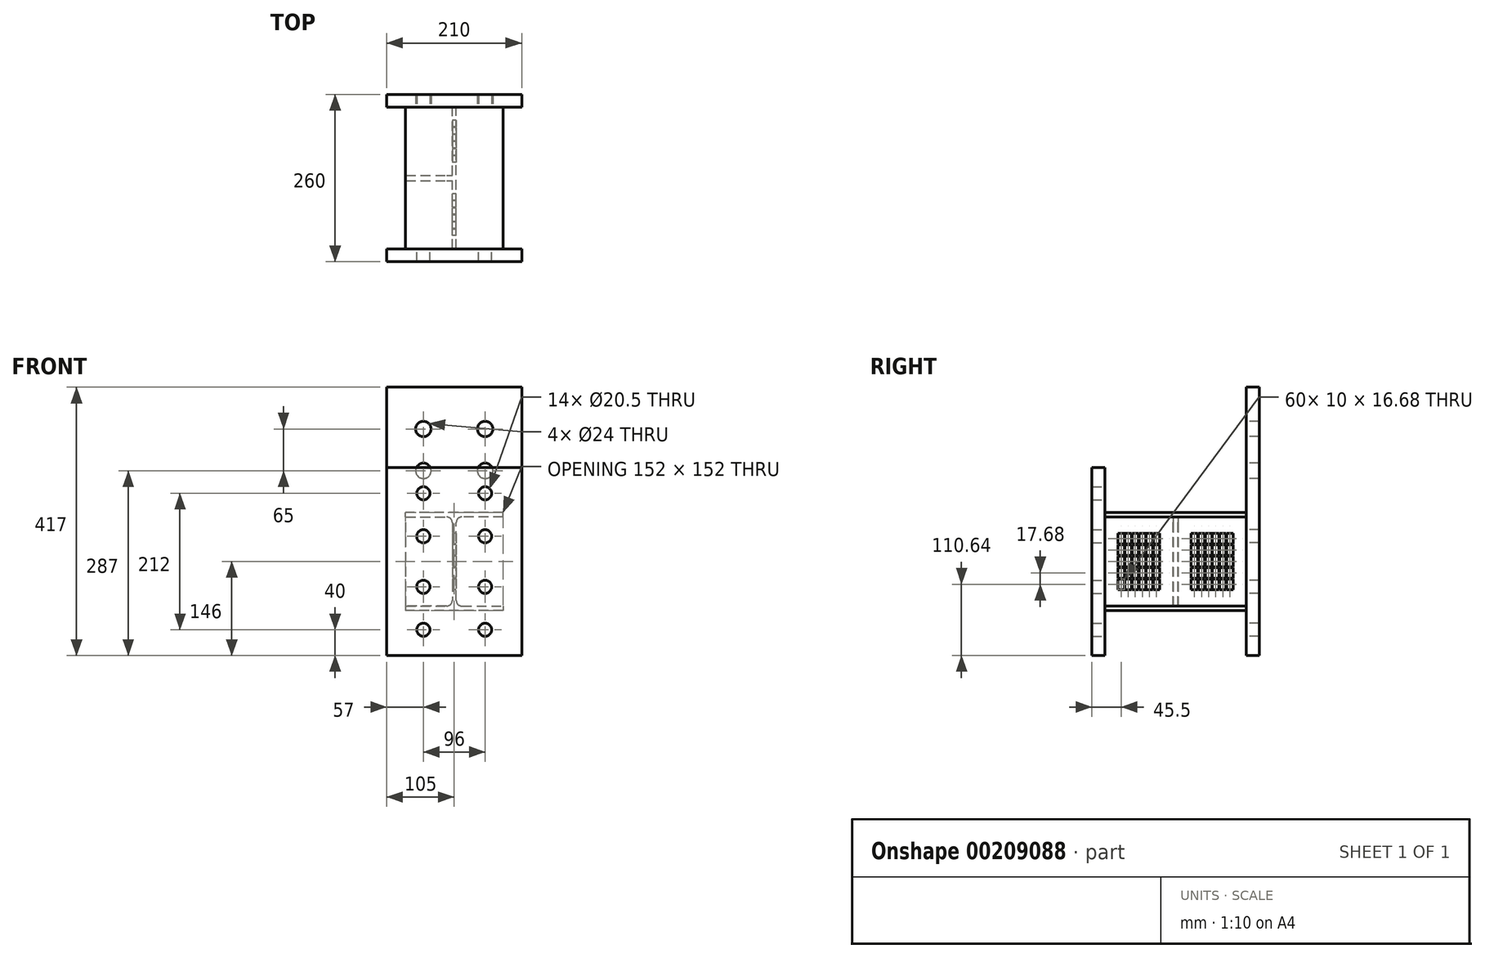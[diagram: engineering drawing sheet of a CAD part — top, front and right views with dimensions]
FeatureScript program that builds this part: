
annotation { "Feature Type Name" : "Feature", "Feature Type Description" : "" }
export const myFeature = defineFeature(function(context is Context, id is Id, definition is map)
    precondition{}
    {
        {
            var Q0;
            Q0=qCreatedBy(makeId("Front.planeOp"),FACE);
            var sketch = newSketch(context, id + "F0", { "sketchPlane" : qUnion([Q0])});
            skLineSegment(sketch, "E0.left", {"start": v(3.05, -60.3) * mm, "end": v(3.05, 60.3) * mm});
            skLineSegment(sketch, "E0.right", {"start": v(-3.05, -60.3) * mm, "end": v(-3.05, 60.3) * mm});
            skPoint(sketch, "E0.middle", {"position": v(0, 0) * mm});
            skLineSegment(sketch, "E1.bottom", {"start": v(76, 69.2) * mm, "end": v(11.95, 69.2) * mm});
            skLineSegment(sketch, "E1.top", {"start": v(76, 76) * mm, "end": v(-76, 76) * mm});
            skLineSegment(sketch, "E1.left", {"start": v(76, 69.2) * mm, "end": v(76, 76) * mm});
            skLineSegment(sketch, "E1.right", {"start": v(-76, 69.2) * mm, "end": v(-76, 76) * mm});
            skLineSegment(sketch, "E2.bottom", {"start": v(-11.95, -69.2) * mm, "end": v(-76, -69.2) * mm});
            skLineSegment(sketch, "E2.top", {"start": v(76, -76) * mm, "end": v(-76, -76) * mm});
            skLineSegment(sketch, "E2.left", {"start": v(76, -69.2) * mm, "end": v(76, -76) * mm});
            skLineSegment(sketch, "E2.right", {"start": v(-76, -69.2) * mm, "end": v(-76, -76) * mm});
            skPoint(sketch, "E3.newPointB", {"position": v(-76, 69.2) * mm});
            skArc(sketch, "E3.filletArc", {"start": v(11.95, 69.2) * mm, "mid": v(5.66, 66.6) * mm, "end": v(3.05, 60.3) * mm});
            skLineSegment(sketch, "E4", {"start": v(-76, 69.2) * mm, "end": v(-11.95, 69.2) * mm});
            skArc(sketch, "E5.filletArc", {"start": v(-3.05, 60.3) * mm, "mid": v(-5.66, 66.6) * mm, "end": v(-11.95, 69.2) * mm});
            skPoint(sketch, "E6.newPointA", {"position": v(76, -69.2) * mm});
            skArc(sketch, "E6.filletArc", {"start": v(-11.95, -69.2) * mm, "mid": v(-5.66, -66.6) * mm, "end": v(-3.05, -60.3) * mm});
            skLineSegment(sketch, "E7", {"start": v(11.95, -69.2) * mm, "end": v(76, -69.2) * mm});
            skArc(sketch, "E8.filletArc", {"start": v(3.05, -60.3) * mm, "mid": v(5.66, -66.6) * mm, "end": v(11.95, -69.2) * mm});
            skSolve(sketch);
        }
        {
            var Q0;
            Q0=qSketchRegion(id+"F0",true);
            extrude(context, id + "F1", {"entities" : qUnion([Q0]), "depth" : 220 * mm, "symmetric" : true});
        }
        {
            var Q0;
            Q0=makeQuery(id+"F1.opExtrude","SWEPT_FACE",FACE,{"disambiguationData":[OSD([sQuery(id+"F0.wireOp",EDGE,"E0.left")])]});
            var sketch = newSketch(context, id + "F2", { "sketchPlane" : qUnion([Q0])});
            skLineSegment(sketch, "E9.bottom", {"start": v(4, -69.2) * mm, "end": v(-4, -69.2) * mm});
            skLineSegment(sketch, "E9.top", {"start": v(4, 69.2) * mm, "end": v(-4, 69.2) * mm});
            skLineSegment(sketch, "E9.left", {"start": v(4, -69.2) * mm, "end": v(4, 69.2) * mm});
            skLineSegment(sketch, "E9.right", {"start": v(-4, -69.2) * mm, "end": v(-4, 69.2) * mm});
            skPoint(sketch, "E9.middle", {"position": v(0, 0) * mm});
            skSolve(sketch);
        }
        {
            var Q0;
            Q0=qSketchRegion(id+"F2",true);
            extrude(context, id + "F3", {"entities" : qUnion([Q0]), "operationType" : NewBodyOperationType.ADD, "oppositeDirection" : true, "depth" : 78.1 * mm});
        }
        {
            var Q0;
            Q0=makeQuery(id+"F1.opExtrude","CAP_FACE",FACE,{"disambiguationData":[OSD([sQuery(id+"F0.wireOp",EDGE,"E0.left"),sQuery(id+"F0.wireOp",EDGE,"E0.right"),sQuery(id+"F0.wireOp",EDGE,"E1.bottom"),sQuery(id+"F0.wireOp",EDGE,"E1.top"),sQuery(id+"F0.wireOp",EDGE,"E1.left"),sQuery(id+"F0.wireOp",EDGE,"E1.right"),sQuery(id+"F0.wireOp",EDGE,"E2.bottom"),sQuery(id+"F0.wireOp",EDGE,"E2.top"),sQuery(id+"F0.wireOp",EDGE,"E2.left"),sQuery(id+"F0.wireOp",EDGE,"E2.right"),sQuery(id+"F0.wireOp",EDGE,"E3.filletArc"),sQuery(id+"F0.wireOp",EDGE,"E4"),sQuery(id+"F0.wireOp",EDGE,"E5.filletArc"),sQuery(id+"F0.wireOp",EDGE,"E6.filletArc"),sQuery(id+"F0.wireOp",EDGE,"E7"),sQuery(id+"F0.wireOp",EDGE,"E8.filletArc")])],"isStart":false});
            var sketch = newSketch(context, id + "F4", { "sketchPlane" : qUnion([Q0])});
            skLineSegment(sketch, "E10.bottom", {"start": v(105, -146) * mm, "end": v(-105, -146) * mm});
            skLineSegment(sketch, "E10.top", {"start": v(105, 146) * mm, "end": v(-105, 146) * mm});
            skLineSegment(sketch, "E10.left", {"start": v(105, -146) * mm, "end": v(105, 146) * mm});
            skLineSegment(sketch, "E10.right", {"start": v(-105, -146) * mm, "end": v(-105, 146) * mm});
            skPoint(sketch, "E10.middle", {"position": v(0, 0) * mm});
            skCircle(sketch, "E11", {"center": v(-48, 106) * mm, "radius": 10.25 * mm});
            skCircle(sketch, "E12", {"center": v(-48, 39.2) * mm, "radius": 10.25 * mm});
            skCircle(sketch, "E13", {"center": v(-48, -39.2) * mm, "radius": 10.25 * mm});
            skCircle(sketch, "E14", {"center": v(-48, -106) * mm, "radius": 10.25 * mm});
            skCircle(sketch, "E15.MirrorC", {"center": v(48, -39.2) * mm, "radius": 10.25 * mm});
            skCircle(sketch, "E16.MirrorC", {"center": v(48, 39.2) * mm, "radius": 10.25 * mm});
            skCircle(sketch, "E17.MirrorC", {"center": v(48, -106) * mm, "radius": 10.25 * mm});
            skCircle(sketch, "E18.MirrorC", {"center": v(48, 106) * mm, "radius": 10.25 * mm});
            skSolve(sketch);
        }
        {
            var Q0;
            Q0=qSketchRegion(id+"F4",true);
            extrude(context, id + "F5", {"entities" : qUnion([Q0]), "operationType" : NewBodyOperationType.ADD, "depth" : 20 * mm});
        }
        {
            var Q0;
            Q0=makeQuery(id+"F1.opExtrude","CAP_FACE",FACE,{"disambiguationData":[OSD([sQuery(id+"F0.wireOp",EDGE,"E0.left"),sQuery(id+"F0.wireOp",EDGE,"E0.right"),sQuery(id+"F0.wireOp",EDGE,"E1.bottom"),sQuery(id+"F0.wireOp",EDGE,"E1.top"),sQuery(id+"F0.wireOp",EDGE,"E1.left"),sQuery(id+"F0.wireOp",EDGE,"E1.right"),sQuery(id+"F0.wireOp",EDGE,"E2.bottom"),sQuery(id+"F0.wireOp",EDGE,"E2.top"),sQuery(id+"F0.wireOp",EDGE,"E2.left"),sQuery(id+"F0.wireOp",EDGE,"E2.right"),sQuery(id+"F0.wireOp",EDGE,"E3.filletArc"),sQuery(id+"F0.wireOp",EDGE,"E4"),sQuery(id+"F0.wireOp",EDGE,"E5.filletArc"),sQuery(id+"F0.wireOp",EDGE,"E6.filletArc"),sQuery(id+"F0.wireOp",EDGE,"E7"),sQuery(id+"F0.wireOp",EDGE,"E8.filletArc")])],"isStart":true});
            var sketch = newSketch(context, id + "F6", { "sketchPlane" : qUnion([Q0])});
            skLineSegment(sketch, "E19.bottom", {"start": v(-105, -146) * mm, "end": v(105, -146) * mm});
            skLineSegment(sketch, "E19.top", {"start": v(-105, 271) * mm, "end": v(105, 271) * mm});
            skLineSegment(sketch, "E19.left", {"start": v(-105, -146) * mm, "end": v(-105, 271) * mm});
            skLineSegment(sketch, "E19.right", {"start": v(105, 271) * mm, "end": v(105, -146) * mm});
            skCircle(sketch, "E20", {"center": v(-48, 39.2) * mm, "radius": 10.25 * mm});
            skCircle(sketch, "E21.MirrorC", {"center": v(-48, -106) * mm, "radius": 10.25 * mm});
            skCircle(sketch, "E22.MirrorC", {"center": v(-48, -39.2) * mm, "radius": 10.25 * mm});
            skLineSegment(sketch, "E23", {"start": v(0, 0) * mm, "end": v(0, 68.37) * mm});
            skPoint(sketch, "E23.endSnap0", {"position": v(0, 76) * mm});
            skCircle(sketch, "E24.MirrorC", {"center": v(48, -106) * mm, "radius": 10.25 * mm});
            skCircle(sketch, "E25.MirrorC", {"center": v(48, -39.2) * mm, "radius": 10.25 * mm});
            skCircle(sketch, "E26.MirrorC", {"center": v(48, 39.2) * mm, "radius": 10.25 * mm});
            skCircle(sketch, "E27", {"center": v(-48, 141) * mm, "radius": 12 * mm});
            skCircle(sketch, "E28", {"center": v(-48, 206) * mm, "radius": 12 * mm});
            skCircle(sketch, "E29.MirrorC", {"center": v(48, 141) * mm, "radius": 12 * mm});
            skCircle(sketch, "E30.MirrorC", {"center": v(48, 206) * mm, "radius": 12 * mm});
            skSolve(sketch);
        }
        {
            var Q0;
            Q0=qSketchRegion(id+"F6",true);
            extrude(context, id + "F7", {"entities" : qUnion([Q0]), "operationType" : NewBodyOperationType.ADD, "depth" : 20 * mm});
        }
        {
            var Q0;
            {var subQ2=sQuery(id+"F0.wireOp",EDGE,"E0.right");Q0=makeQuery(id+"F3.boolean.opBoolean","SPLIT",FACE,{"disambiguationData":[TD([makeQuery(id+"F3.opExtrude","SWEPT_FACE",FACE,{"disambiguationData":[OSD([sQuery(id+"F2.wireOp",EDGE,"E9.left")])]})])],"derivedFrom":makeQuery(id+"F1.opExtrude","SWEPT_FACE",FACE,{"disambiguationData":[OSD([subQ2])]})});}
            var sketch = newSketch(context, id + "F8", { "sketchPlane" : qUnion([Q0])});
            skPoint(sketch, "E31.middle", {"position": v(-57, 0) * mm});
            skPoint(sketch, "E31.middle.positionSnap0", {"position": v(-4, 0) * mm});
            skPoint(sketch, "E31.middle.positionSnap1", {"position": v(-57, 60.3) * mm});
            skPoint(sketch, "E31.centerSnap0", {"position": v(-4, 0) * mm});
            skPoint(sketch, "E31.centerSnap1", {"position": v(-57, 60.3) * mm});
            skPoint(sketch, "E32.MirrorP", {"position": v(-35, 0) * mm});
            skPoint(sketch, "E33.middle", {"position": v(-57, 26.52) * mm});
            skPoint(sketch, "E34.middle", {"position": v(-57, 8.84) * mm});
            skPoint(sketch, "E35.middle", {"position": v(-57, -8.84) * mm});
            skPoint(sketch, "E36.middle", {"position": v(-57, -26.52) * mm});
            skPoint(sketch, "E37.middle", {"position": v(-57, -44.2) * mm});
            skPoint(sketch, "E38.middle", {"position": v(-57, 44.2) * mm});
            skPoint(sketch, "E39.middle", {"position": v(-90, 0) * mm});
            skPoint(sketch, "E40.middle", {"position": v(-79, 0) * mm});
            skPoint(sketch, "E41.middle", {"position": v(-68, 0) * mm});
            skPoint(sketch, "E42.middle", {"position": v(-46, 0) * mm});
            skPoint(sketch, "E43.middle", {"position": v(-24, 0) * mm});
            skLineSegment(sketch, "E44.bottom", {"start": v(-89.5, 43.7) * mm, "end": v(-79.5, 43.7) * mm});
            skLineSegment(sketch, "E44.top", {"start": v(-89.5, 27.02) * mm, "end": v(-79.5, 27.02) * mm});
            skLineSegment(sketch, "E44.left", {"start": v(-89.5, 43.7) * mm, "end": v(-89.5, 27.02) * mm});
            skLineSegment(sketch, "E44.right", {"start": v(-79.5, 43.7) * mm, "end": v(-79.5, 27.02) * mm});
            skLineSegment(sketch, "E45.bottom", {"start": v(-78.5, 43.7) * mm, "end": v(-68.5, 43.7) * mm});
            skLineSegment(sketch, "E45.top", {"start": v(-78.5, 27.02) * mm, "end": v(-68.5, 27.02) * mm});
            skLineSegment(sketch, "E45.left", {"start": v(-78.5, 43.7) * mm, "end": v(-78.5, 27.02) * mm});
            skLineSegment(sketch, "E45.right", {"start": v(-68.5, 43.7) * mm, "end": v(-68.5, 27.02) * mm});
            skLineSegment(sketch, "E46.bottom", {"start": v(-67.5, 43.7) * mm, "end": v(-57.5, 43.7) * mm});
            skLineSegment(sketch, "E46.top", {"start": v(-67.5, 27.02) * mm, "end": v(-57.5, 27.02) * mm});
            skLineSegment(sketch, "E46.left", {"start": v(-67.5, 43.7) * mm, "end": v(-67.5, 27.02) * mm});
            skLineSegment(sketch, "E46.right", {"start": v(-57.5, 43.7) * mm, "end": v(-57.5, 27.02) * mm});
            skLineSegment(sketch, "E47.bottom", {"start": v(-56.5, 43.7) * mm, "end": v(-46.5, 43.7) * mm});
            skLineSegment(sketch, "E47.top", {"start": v(-56.5, 27.02) * mm, "end": v(-46.5, 27.02) * mm});
            skLineSegment(sketch, "E47.left", {"start": v(-56.5, 43.7) * mm, "end": v(-56.5, 27.02) * mm});
            skLineSegment(sketch, "E47.right", {"start": v(-46.5, 43.7) * mm, "end": v(-46.5, 27.02) * mm});
            skLineSegment(sketch, "E48.bottom", {"start": v(-45.5, 43.7) * mm, "end": v(-35.5, 43.7) * mm});
            skLineSegment(sketch, "E48.top", {"start": v(-45.5, 27.02) * mm, "end": v(-35.5, 27.02) * mm});
            skLineSegment(sketch, "E48.left", {"start": v(-45.5, 43.7) * mm, "end": v(-45.5, 27.02) * mm});
            skLineSegment(sketch, "E48.right", {"start": v(-35.5, 43.7) * mm, "end": v(-35.5, 27.02) * mm});
            skLineSegment(sketch, "E49.bottom", {"start": v(-34.5, 43.7) * mm, "end": v(-24.5, 43.7) * mm});
            skLineSegment(sketch, "E49.top", {"start": v(-34.5, 27.02) * mm, "end": v(-24.5, 27.02) * mm});
            skLineSegment(sketch, "E49.left", {"start": v(-34.5, 43.7) * mm, "end": v(-34.5, 27.02) * mm});
            skLineSegment(sketch, "E49.right", {"start": v(-24.5, 43.7) * mm, "end": v(-24.5, 27.02) * mm});
            skLineSegment(sketch, "E50.bottom", {"start": v(-89.5, 26.02) * mm, "end": v(-79.5, 26.02) * mm});
            skLineSegment(sketch, "E50.top", {"start": v(-89.5, 9.34) * mm, "end": v(-79.5, 9.34) * mm});
            skLineSegment(sketch, "E50.left", {"start": v(-89.5, 26.02) * mm, "end": v(-89.5, 9.34) * mm});
            skLineSegment(sketch, "E50.right", {"start": v(-79.5, 26.02) * mm, "end": v(-79.5, 9.34) * mm});
            skLineSegment(sketch, "E51.bottom", {"start": v(-78.5, 26.02) * mm, "end": v(-68.5, 26.02) * mm});
            skLineSegment(sketch, "E51.top", {"start": v(-78.5, 9.34) * mm, "end": v(-68.5, 9.34) * mm});
            skLineSegment(sketch, "E51.left", {"start": v(-78.5, 26.02) * mm, "end": v(-78.5, 9.34) * mm});
            skLineSegment(sketch, "E51.right", {"start": v(-68.5, 26.02) * mm, "end": v(-68.5, 9.34) * mm});
            skLineSegment(sketch, "E52.bottom", {"start": v(-67.5, 26.02) * mm, "end": v(-57.5, 26.02) * mm});
            skLineSegment(sketch, "E52.top", {"start": v(-67.5, 9.34) * mm, "end": v(-57.5, 9.34) * mm});
            skLineSegment(sketch, "E52.left", {"start": v(-67.5, 26.02) * mm, "end": v(-67.5, 9.34) * mm});
            skLineSegment(sketch, "E52.right", {"start": v(-57.5, 26.02) * mm, "end": v(-57.5, 9.34) * mm});
            skLineSegment(sketch, "E53.bottom", {"start": v(-56.5, 26.02) * mm, "end": v(-46.5, 26.02) * mm});
            skLineSegment(sketch, "E53.top", {"start": v(-56.5, 9.34) * mm, "end": v(-46.5, 9.34) * mm});
            skLineSegment(sketch, "E53.left", {"start": v(-56.5, 26.02) * mm, "end": v(-56.5, 9.34) * mm});
            skLineSegment(sketch, "E53.right", {"start": v(-46.5, 26.02) * mm, "end": v(-46.5, 9.34) * mm});
            skLineSegment(sketch, "E54.bottom", {"start": v(-45.5, 26.02) * mm, "end": v(-35.5, 26.02) * mm});
            skLineSegment(sketch, "E54.top", {"start": v(-45.5, 9.34) * mm, "end": v(-35.5, 9.34) * mm});
            skLineSegment(sketch, "E54.left", {"start": v(-45.5, 26.02) * mm, "end": v(-45.5, 9.34) * mm});
            skLineSegment(sketch, "E54.right", {"start": v(-35.5, 26.02) * mm, "end": v(-35.5, 9.34) * mm});
            skLineSegment(sketch, "E55.bottom", {"start": v(-34.5, 26.02) * mm, "end": v(-24.5, 26.02) * mm});
            skLineSegment(sketch, "E55.top", {"start": v(-34.5, 9.34) * mm, "end": v(-24.5, 9.34) * mm});
            skLineSegment(sketch, "E55.left", {"start": v(-34.5, 26.02) * mm, "end": v(-34.5, 9.34) * mm});
            skLineSegment(sketch, "E55.right", {"start": v(-24.5, 26.02) * mm, "end": v(-24.5, 9.34) * mm});
            skLineSegment(sketch, "E56.bottom", {"start": v(-89.5, 8.34) * mm, "end": v(-79.5, 8.34) * mm});
            skLineSegment(sketch, "E56.top", {"start": v(-89.5, -8.34) * mm, "end": v(-79.5, -8.34) * mm});
            skLineSegment(sketch, "E56.left", {"start": v(-89.5, 8.34) * mm, "end": v(-89.5, -8.34) * mm});
            skLineSegment(sketch, "E56.right", {"start": v(-79.5, 8.34) * mm, "end": v(-79.5, -8.34) * mm});
            skLineSegment(sketch, "E57.bottom", {"start": v(-78.5, 8.34) * mm, "end": v(-68.5, 8.34) * mm});
            skLineSegment(sketch, "E57.top", {"start": v(-78.5, -8.34) * mm, "end": v(-68.5, -8.34) * mm});
            skLineSegment(sketch, "E57.left", {"start": v(-78.5, 8.34) * mm, "end": v(-78.5, -8.34) * mm});
            skLineSegment(sketch, "E57.right", {"start": v(-68.5, 8.34) * mm, "end": v(-68.5, -8.34) * mm});
            skLineSegment(sketch, "E58.bottom", {"start": v(-67.5, 8.34) * mm, "end": v(-57.5, 8.34) * mm});
            skLineSegment(sketch, "E58.top", {"start": v(-67.5, -8.34) * mm, "end": v(-57.5, -8.34) * mm});
            skLineSegment(sketch, "E58.left", {"start": v(-67.5, 8.34) * mm, "end": v(-67.5, -8.34) * mm});
            skLineSegment(sketch, "E58.right", {"start": v(-57.5, 8.34) * mm, "end": v(-57.5, -8.34) * mm});
            skLineSegment(sketch, "E59.bottom", {"start": v(-56.5, 8.34) * mm, "end": v(-46.5, 8.34) * mm});
            skLineSegment(sketch, "E59.top", {"start": v(-56.5, -8.34) * mm, "end": v(-46.5, -8.34) * mm});
            skLineSegment(sketch, "E59.left", {"start": v(-56.5, 8.34) * mm, "end": v(-56.5, -8.34) * mm});
            skLineSegment(sketch, "E59.right", {"start": v(-46.5, 8.34) * mm, "end": v(-46.5, -8.34) * mm});
            skLineSegment(sketch, "E60.bottom", {"start": v(-45.5, 8.34) * mm, "end": v(-35.5, 8.34) * mm});
            skLineSegment(sketch, "E60.top", {"start": v(-45.5, -8.34) * mm, "end": v(-35.5, -8.34) * mm});
            skLineSegment(sketch, "E60.left", {"start": v(-45.5, 8.34) * mm, "end": v(-45.5, -8.34) * mm});
            skLineSegment(sketch, "E60.right", {"start": v(-35.5, 8.34) * mm, "end": v(-35.5, -8.34) * mm});
            skLineSegment(sketch, "E61.bottom", {"start": v(-34.5, 8.34) * mm, "end": v(-24.5, 8.34) * mm});
            skLineSegment(sketch, "E61.top", {"start": v(-34.5, -8.34) * mm, "end": v(-24.5, -8.34) * mm});
            skLineSegment(sketch, "E61.left", {"start": v(-34.5, 8.34) * mm, "end": v(-34.5, -8.34) * mm});
            skLineSegment(sketch, "E61.right", {"start": v(-24.5, 8.34) * mm, "end": v(-24.5, -8.34) * mm});
            skLineSegment(sketch, "E62.bottom", {"start": v(-89.5, -9.34) * mm, "end": v(-79.5, -9.34) * mm});
            skLineSegment(sketch, "E62.top", {"start": v(-89.5, -26.02) * mm, "end": v(-79.5, -26.02) * mm});
            skLineSegment(sketch, "E62.left", {"start": v(-89.5, -9.34) * mm, "end": v(-89.5, -26.02) * mm});
            skLineSegment(sketch, "E62.right", {"start": v(-79.5, -9.34) * mm, "end": v(-79.5, -26.02) * mm});
            skLineSegment(sketch, "E63.bottom", {"start": v(-78.5, -9.34) * mm, "end": v(-68.5, -9.34) * mm});
            skLineSegment(sketch, "E63.top", {"start": v(-78.5, -26.02) * mm, "end": v(-68.5, -26.02) * mm});
            skLineSegment(sketch, "E63.left", {"start": v(-78.5, -9.34) * mm, "end": v(-78.5, -26.02) * mm});
            skLineSegment(sketch, "E63.right", {"start": v(-68.5, -9.34) * mm, "end": v(-68.5, -26.02) * mm});
            skLineSegment(sketch, "E64.bottom", {"start": v(-67.5, -9.34) * mm, "end": v(-57.5, -9.34) * mm});
            skLineSegment(sketch, "E64.top", {"start": v(-67.5, -26.02) * mm, "end": v(-57.5, -26.02) * mm});
            skLineSegment(sketch, "E64.left", {"start": v(-67.5, -9.34) * mm, "end": v(-67.5, -26.02) * mm});
            skLineSegment(sketch, "E64.right", {"start": v(-57.5, -9.34) * mm, "end": v(-57.5, -26.02) * mm});
            skLineSegment(sketch, "E65.bottom", {"start": v(-56.5, -9.34) * mm, "end": v(-46.5, -9.34) * mm});
            skLineSegment(sketch, "E65.top", {"start": v(-56.5, -26.02) * mm, "end": v(-46.5, -26.02) * mm});
            skLineSegment(sketch, "E65.left", {"start": v(-56.5, -9.34) * mm, "end": v(-56.5, -26.02) * mm});
            skLineSegment(sketch, "E65.right", {"start": v(-46.5, -9.34) * mm, "end": v(-46.5, -26.02) * mm});
            skLineSegment(sketch, "E66.bottom", {"start": v(-45.5, -9.34) * mm, "end": v(-35.5, -9.34) * mm});
            skLineSegment(sketch, "E66.top", {"start": v(-45.5, -26.02) * mm, "end": v(-35.5, -26.02) * mm});
            skLineSegment(sketch, "E66.left", {"start": v(-45.5, -9.34) * mm, "end": v(-45.5, -26.02) * mm});
            skLineSegment(sketch, "E66.right", {"start": v(-35.5, -9.34) * mm, "end": v(-35.5, -26.02) * mm});
            skLineSegment(sketch, "E67.bottom", {"start": v(-34.5, -9.34) * mm, "end": v(-24.5, -9.34) * mm});
            skLineSegment(sketch, "E67.top", {"start": v(-34.5, -26.02) * mm, "end": v(-24.5, -26.02) * mm});
            skLineSegment(sketch, "E67.left", {"start": v(-34.5, -9.34) * mm, "end": v(-34.5, -26.02) * mm});
            skLineSegment(sketch, "E67.right", {"start": v(-24.5, -9.34) * mm, "end": v(-24.5, -26.02) * mm});
            skLineSegment(sketch, "E68.bottom", {"start": v(-89.5, -27.02) * mm, "end": v(-79.5, -27.02) * mm});
            skLineSegment(sketch, "E68.top", {"start": v(-89.5, -43.7) * mm, "end": v(-79.5, -43.7) * mm});
            skLineSegment(sketch, "E68.left", {"start": v(-89.5, -27.02) * mm, "end": v(-89.5, -43.7) * mm});
            skLineSegment(sketch, "E68.right", {"start": v(-79.5, -27.02) * mm, "end": v(-79.5, -43.7) * mm});
            skLineSegment(sketch, "E69.bottom", {"start": v(-78.5, -27.02) * mm, "end": v(-68.5, -27.02) * mm});
            skLineSegment(sketch, "E69.top", {"start": v(-78.5, -43.7) * mm, "end": v(-68.5, -43.7) * mm});
            skLineSegment(sketch, "E69.left", {"start": v(-78.5, -27.02) * mm, "end": v(-78.5, -43.7) * mm});
            skLineSegment(sketch, "E69.right", {"start": v(-68.5, -27.02) * mm, "end": v(-68.5, -43.7) * mm});
            skLineSegment(sketch, "E70.bottom", {"start": v(-67.5, -27.02) * mm, "end": v(-57.5, -27.02) * mm});
            skLineSegment(sketch, "E70.top", {"start": v(-67.5, -43.7) * mm, "end": v(-57.5, -43.7) * mm});
            skLineSegment(sketch, "E70.left", {"start": v(-67.5, -27.02) * mm, "end": v(-67.5, -43.7) * mm});
            skLineSegment(sketch, "E70.right", {"start": v(-57.5, -27.02) * mm, "end": v(-57.5, -43.7) * mm});
            skLineSegment(sketch, "E71.bottom", {"start": v(-56.5, -27.02) * mm, "end": v(-46.5, -27.02) * mm});
            skLineSegment(sketch, "E71.top", {"start": v(-56.5, -43.7) * mm, "end": v(-46.5, -43.7) * mm});
            skLineSegment(sketch, "E71.left", {"start": v(-56.5, -27.02) * mm, "end": v(-56.5, -43.7) * mm});
            skLineSegment(sketch, "E71.right", {"start": v(-46.5, -27.02) * mm, "end": v(-46.5, -43.7) * mm});
            skLineSegment(sketch, "E72.bottom", {"start": v(-45.5, -27.02) * mm, "end": v(-35.5, -27.02) * mm});
            skLineSegment(sketch, "E72.top", {"start": v(-45.5, -43.7) * mm, "end": v(-35.5, -43.7) * mm});
            skLineSegment(sketch, "E72.left", {"start": v(-45.5, -27.02) * mm, "end": v(-45.5, -43.7) * mm});
            skLineSegment(sketch, "E72.right", {"start": v(-35.5, -27.02) * mm, "end": v(-35.5, -43.7) * mm});
            skLineSegment(sketch, "E73.bottom", {"start": v(-34.5, -27.02) * mm, "end": v(-24.5, -27.02) * mm});
            skLineSegment(sketch, "E73.top", {"start": v(-34.5, -43.7) * mm, "end": v(-24.5, -43.7) * mm});
            skLineSegment(sketch, "E73.left", {"start": v(-34.5, -27.02) * mm, "end": v(-34.5, -43.7) * mm});
            skLineSegment(sketch, "E73.right", {"start": v(-24.5, -27.02) * mm, "end": v(-24.5, -43.7) * mm});
            skLineSegment(sketch, "E74", {"start": v(0, 60.3) * mm, "end": v(0, -69) * mm});
            skLineSegment(sketch, "E75.MirrorCS", {"start": v(35.5, 8.34) * mm, "end": v(35.5, -8.34) * mm});
            skLineSegment(sketch, "E76.MirrorCS", {"start": v(79.5, 8.34) * mm, "end": v(79.5, -8.34) * mm});
            skLineSegment(sketch, "E77.MirrorCS", {"start": v(57.5, 8.34) * mm, "end": v(57.5, -8.34) * mm});
            skLineSegment(sketch, "E78.MirrorCS", {"start": v(34.5, 8.34) * mm, "end": v(34.5, -8.34) * mm});
            skLineSegment(sketch, "E79.MirrorCS", {"start": v(67.5, -27.02) * mm, "end": v(57.5, -27.02) * mm});
            skLineSegment(sketch, "E80.MirrorCS", {"start": v(56.5, 8.34) * mm, "end": v(56.5, -8.34) * mm});
            skLineSegment(sketch, "E81.MirrorCS", {"start": v(45.5, 8.34) * mm, "end": v(45.5, -8.34) * mm});
            skLineSegment(sketch, "E82.MirrorCS", {"start": v(89.5, 8.34) * mm, "end": v(89.5, -8.34) * mm});
            skPoint(sketch, "E83.MirrorP", {"position": v(57, 0) * mm});
            skLineSegment(sketch, "E84.MirrorCS", {"start": v(79.5, 43.7) * mm, "end": v(79.5, 27.02) * mm});
            skLineSegment(sketch, "E85.MirrorCS", {"start": v(67.5, 43.7) * mm, "end": v(57.5, 43.7) * mm});
            skLineSegment(sketch, "E86.MirrorCS", {"start": v(67.5, 27.02) * mm, "end": v(57.5, 27.02) * mm});
            skLineSegment(sketch, "E87.MirrorCS", {"start": v(79.5, -27.02) * mm, "end": v(79.5, -43.7) * mm});
            skPoint(sketch, "E88.MirrorP", {"position": v(35, 0) * mm});
            skLineSegment(sketch, "E89.MirrorCS", {"start": v(34.5, -27.02) * mm, "end": v(24.5, -27.02) * mm});
            skLineSegment(sketch, "E90.MirrorCS", {"start": v(78.5, -27.02) * mm, "end": v(68.5, -27.02) * mm});
            skLineSegment(sketch, "E91.MirrorCS", {"start": v(56.5, -26.02) * mm, "end": v(46.5, -26.02) * mm});
            skLineSegment(sketch, "E92.MirrorCS", {"start": v(78.5, 8.34) * mm, "end": v(78.5, -8.34) * mm});
            skLineSegment(sketch, "E93.MirrorCS", {"start": v(24.5, 8.34) * mm, "end": v(24.5, -8.34) * mm});
            skLineSegment(sketch, "E94.MirrorCS", {"start": v(68.5, 8.34) * mm, "end": v(68.5, -8.34) * mm});
            skLineSegment(sketch, "E95.MirrorCS", {"start": v(67.5, 8.34) * mm, "end": v(57.5, 8.34) * mm});
            skLineSegment(sketch, "E96.MirrorCS", {"start": v(89.5, -26.02) * mm, "end": v(79.5, -26.02) * mm});
            skLineSegment(sketch, "E97.MirrorCS", {"start": v(67.5, -8.34) * mm, "end": v(57.5, -8.34) * mm});
            skLineSegment(sketch, "E98.MirrorCS", {"start": v(67.5, -43.7) * mm, "end": v(57.5, -43.7) * mm});
            skLineSegment(sketch, "E99.MirrorCS", {"start": v(45.5, -26.02) * mm, "end": v(35.5, -26.02) * mm});
            skLineSegment(sketch, "E100.MirrorCS", {"start": v(67.5, 8.34) * mm, "end": v(67.5, -8.34) * mm});
            skLineSegment(sketch, "E101.MirrorCS", {"start": v(79.5, -9.34) * mm, "end": v(79.5, -26.02) * mm});
            skLineSegment(sketch, "E102.MirrorCS", {"start": v(79.5, 26.02) * mm, "end": v(79.5, 9.34) * mm});
            skLineSegment(sketch, "E103.MirrorCS", {"start": v(46.5, 8.34) * mm, "end": v(46.5, -8.34) * mm});
            skLineSegment(sketch, "E104.MirrorCS", {"start": v(67.5, 26.02) * mm, "end": v(57.5, 26.02) * mm});
            skLineSegment(sketch, "E105.MirrorCS", {"start": v(67.5, -9.34) * mm, "end": v(57.5, -9.34) * mm});
            skLineSegment(sketch, "E106.MirrorCS", {"start": v(67.5, 9.34) * mm, "end": v(57.5, 9.34) * mm});
            skLineSegment(sketch, "E107.MirrorCS", {"start": v(67.5, -26.02) * mm, "end": v(57.5, -26.02) * mm});
            skLineSegment(sketch, "E108.MirrorCS", {"start": v(67.5, 26.02) * mm, "end": v(67.5, 9.34) * mm});
            skLineSegment(sketch, "E109.MirrorCS", {"start": v(45.5, 43.7) * mm, "end": v(45.5, 27.02) * mm});
            skLineSegment(sketch, "E110.MirrorCS", {"start": v(89.5, -27.02) * mm, "end": v(89.5, -43.7) * mm});
            skLineSegment(sketch, "E111.MirrorCS", {"start": v(67.5, -9.34) * mm, "end": v(67.5, -26.02) * mm});
            skLineSegment(sketch, "E112.MirrorCS", {"start": v(45.5, -27.02) * mm, "end": v(45.5, -43.7) * mm});
            skLineSegment(sketch, "E113.MirrorCS", {"start": v(56.5, 27.02) * mm, "end": v(46.5, 27.02) * mm});
            skLineSegment(sketch, "E114.MirrorCS", {"start": v(56.5, 43.7) * mm, "end": v(56.5, 27.02) * mm});
            skLineSegment(sketch, "E115.MirrorCS", {"start": v(46.5, 43.7) * mm, "end": v(46.5, 27.02) * mm});
            skLineSegment(sketch, "E116.MirrorCS", {"start": v(89.5, 43.7) * mm, "end": v(79.5, 43.7) * mm});
            skLineSegment(sketch, "E117.MirrorCS", {"start": v(89.5, 27.02) * mm, "end": v(79.5, 27.02) * mm});
            skLineSegment(sketch, "E118.MirrorCS", {"start": v(89.5, 43.7) * mm, "end": v(89.5, 27.02) * mm});
            skLineSegment(sketch, "E119.MirrorCS", {"start": v(78.5, 43.7) * mm, "end": v(68.5, 43.7) * mm});
            skLineSegment(sketch, "E120.MirrorCS", {"start": v(78.5, 27.02) * mm, "end": v(68.5, 27.02) * mm});
            skLineSegment(sketch, "E121.MirrorCS", {"start": v(57.5, -9.34) * mm, "end": v(57.5, -26.02) * mm});
            skLineSegment(sketch, "E122.MirrorCS", {"start": v(67.5, 43.7) * mm, "end": v(67.5, 27.02) * mm});
            skLineSegment(sketch, "E123.MirrorCS", {"start": v(35.5, -27.02) * mm, "end": v(35.5, -43.7) * mm});
            skLineSegment(sketch, "E124.MirrorCS", {"start": v(57.5, 43.7) * mm, "end": v(57.5, 27.02) * mm});
            skLineSegment(sketch, "E125.MirrorCS", {"start": v(56.5, 43.7) * mm, "end": v(46.5, 43.7) * mm});
            skLineSegment(sketch, "E126.MirrorCS", {"start": v(57.5, 26.02) * mm, "end": v(57.5, 9.34) * mm});
            skLineSegment(sketch, "E127.MirrorCS", {"start": v(35.5, 43.7) * mm, "end": v(35.5, 27.02) * mm});
            skPoint(sketch, "E128.MirrorP", {"position": v(24, 0) * mm});
            skLineSegment(sketch, "E129.MirrorCS", {"start": v(34.5, 43.7) * mm, "end": v(24.5, 43.7) * mm});
            skLineSegment(sketch, "E130.MirrorCS", {"start": v(56.5, -9.34) * mm, "end": v(46.5, -9.34) * mm});
            skLineSegment(sketch, "E131.MirrorCS", {"start": v(34.5, 8.34) * mm, "end": v(24.5, 8.34) * mm});
            skLineSegment(sketch, "E132.MirrorCS", {"start": v(78.5, 26.02) * mm, "end": v(68.5, 26.02) * mm});
            skPoint(sketch, "E133.MirrorP", {"position": v(46, 0) * mm});
            skLineSegment(sketch, "E134.MirrorCS", {"start": v(78.5, 43.7) * mm, "end": v(78.5, 27.02) * mm});
            skLineSegment(sketch, "E135.MirrorCS", {"start": v(68.5, 43.7) * mm, "end": v(68.5, 27.02) * mm});
            skLineSegment(sketch, "E136.MirrorCS", {"start": v(56.5, 26.02) * mm, "end": v(46.5, 26.02) * mm});
            skLineSegment(sketch, "E137.MirrorCS", {"start": v(78.5, 8.34) * mm, "end": v(68.5, 8.34) * mm});
            skLineSegment(sketch, "E138.MirrorCS", {"start": v(56.5, 9.34) * mm, "end": v(46.5, 9.34) * mm});
            skLineSegment(sketch, "E139.MirrorCS", {"start": v(34.5, 27.02) * mm, "end": v(24.5, 27.02) * mm});
            skLineSegment(sketch, "E140.MirrorCS", {"start": v(78.5, -43.7) * mm, "end": v(68.5, -43.7) * mm});
            skLineSegment(sketch, "E141.MirrorCS", {"start": v(34.5, -8.34) * mm, "end": v(24.5, -8.34) * mm});
            skLineSegment(sketch, "E142.MirrorCS", {"start": v(34.5, -43.7) * mm, "end": v(24.5, -43.7) * mm});
            skLineSegment(sketch, "E143.MirrorCS", {"start": v(78.5, -8.34) * mm, "end": v(68.5, -8.34) * mm});
            skLineSegment(sketch, "E144.MirrorCS", {"start": v(34.5, 43.7) * mm, "end": v(34.5, 27.02) * mm});
            skLineSegment(sketch, "E145.MirrorCS", {"start": v(56.5, 26.02) * mm, "end": v(56.5, 9.34) * mm});
            skLineSegment(sketch, "E146.MirrorCS", {"start": v(78.5, -27.02) * mm, "end": v(78.5, -43.7) * mm});
            skLineSegment(sketch, "E147.MirrorCS", {"start": v(56.5, -9.34) * mm, "end": v(56.5, -26.02) * mm});
            skLineSegment(sketch, "E148.MirrorCS", {"start": v(34.5, -27.02) * mm, "end": v(34.5, -43.7) * mm});
            skLineSegment(sketch, "E149.MirrorCS", {"start": v(46.5, 26.02) * mm, "end": v(46.5, 9.34) * mm});
            skLineSegment(sketch, "E150.MirrorCS", {"start": v(24.5, 43.7) * mm, "end": v(24.5, 27.02) * mm});
            skLineSegment(sketch, "E151.MirrorCS", {"start": v(24.5, -27.02) * mm, "end": v(24.5, -43.7) * mm});
            skLineSegment(sketch, "E152.MirrorCS", {"start": v(68.5, -27.02) * mm, "end": v(68.5, -43.7) * mm});
            skLineSegment(sketch, "E153.MirrorCS", {"start": v(46.5, -9.34) * mm, "end": v(46.5, -26.02) * mm});
            skPoint(sketch, "E154.MirrorP", {"position": v(57, 26.52) * mm});
            skLineSegment(sketch, "E155.MirrorCS", {"start": v(89.5, -9.34) * mm, "end": v(79.5, -9.34) * mm});
            skLineSegment(sketch, "E156.MirrorCS", {"start": v(45.5, 26.02) * mm, "end": v(35.5, 26.02) * mm});
            skLineSegment(sketch, "E157.MirrorCS", {"start": v(89.5, 26.02) * mm, "end": v(79.5, 26.02) * mm});
            skLineSegment(sketch, "E158.MirrorCS", {"start": v(45.5, -9.34) * mm, "end": v(35.5, -9.34) * mm});
            skPoint(sketch, "E159.MirrorP", {"position": v(57, 8.84) * mm});
            skLineSegment(sketch, "E160.MirrorCS", {"start": v(45.5, 9.34) * mm, "end": v(35.5, 9.34) * mm});
            skLineSegment(sketch, "E161.MirrorCS", {"start": v(89.5, 9.34) * mm, "end": v(79.5, 9.34) * mm});
            skPoint(sketch, "E162.MirrorP", {"position": v(57, -8.84) * mm});
            skLineSegment(sketch, "E163.MirrorCS", {"start": v(89.5, -9.34) * mm, "end": v(89.5, -26.02) * mm});
            skLineSegment(sketch, "E164.MirrorCS", {"start": v(45.5, 26.02) * mm, "end": v(45.5, 9.34) * mm});
            skLineSegment(sketch, "E165.MirrorCS", {"start": v(89.5, 26.02) * mm, "end": v(89.5, 9.34) * mm});
            skLineSegment(sketch, "E166.MirrorCS", {"start": v(67.5, -27.02) * mm, "end": v(67.5, -43.7) * mm});
            skLineSegment(sketch, "E167.MirrorCS", {"start": v(45.5, -9.34) * mm, "end": v(45.5, -26.02) * mm});
            skLineSegment(sketch, "E168.MirrorCS", {"start": v(56.5, -43.7) * mm, "end": v(46.5, -43.7) * mm});
            skPoint(sketch, "E169.MirrorP", {"position": v(57, -26.52) * mm});
            skLineSegment(sketch, "E170.MirrorCS", {"start": v(35.5, 26.02) * mm, "end": v(35.5, 9.34) * mm});
            skLineSegment(sketch, "E171.MirrorCS", {"start": v(57.5, -27.02) * mm, "end": v(57.5, -43.7) * mm});
            skLineSegment(sketch, "E172.MirrorCS", {"start": v(35.5, -9.34) * mm, "end": v(35.5, -26.02) * mm});
            skPoint(sketch, "E173.MirrorP", {"position": v(57, 44.2) * mm});
            skLineSegment(sketch, "E174.MirrorCS", {"start": v(78.5, 9.34) * mm, "end": v(68.5, 9.34) * mm});
            skLineSegment(sketch, "E175.MirrorCS", {"start": v(34.5, -26.02) * mm, "end": v(24.5, -26.02) * mm});
            skLineSegment(sketch, "E176.MirrorCS", {"start": v(78.5, -26.02) * mm, "end": v(68.5, -26.02) * mm});
            skLineSegment(sketch, "E177.MirrorCS", {"start": v(56.5, -8.34) * mm, "end": v(46.5, -8.34) * mm});
            skLineSegment(sketch, "E178.MirrorCS", {"start": v(34.5, 9.34) * mm, "end": v(24.5, 9.34) * mm});
            skPoint(sketch, "E179.MirrorP", {"position": v(57, -44.2) * mm});
            skLineSegment(sketch, "E180.MirrorCS", {"start": v(78.5, -9.34) * mm, "end": v(68.5, -9.34) * mm});
            skLineSegment(sketch, "E181.MirrorCS", {"start": v(34.5, 26.02) * mm, "end": v(24.5, 26.02) * mm});
            skLineSegment(sketch, "E182.MirrorCS", {"start": v(56.5, 8.34) * mm, "end": v(46.5, 8.34) * mm});
            skLineSegment(sketch, "E183.MirrorCS", {"start": v(56.5, -27.02) * mm, "end": v(46.5, -27.02) * mm});
            skLineSegment(sketch, "E184.MirrorCS", {"start": v(34.5, -9.34) * mm, "end": v(24.5, -9.34) * mm});
            skPoint(sketch, "E185.MirrorP", {"position": v(90, 0) * mm});
            skLineSegment(sketch, "E186.MirrorCS", {"start": v(78.5, 26.02) * mm, "end": v(78.5, 9.34) * mm});
            skLineSegment(sketch, "E187.MirrorCS", {"start": v(34.5, -9.34) * mm, "end": v(34.5, -26.02) * mm});
            skLineSegment(sketch, "E188.MirrorCS", {"start": v(78.5, -9.34) * mm, "end": v(78.5, -26.02) * mm});
            skLineSegment(sketch, "E189.MirrorCS", {"start": v(34.5, 26.02) * mm, "end": v(34.5, 9.34) * mm});
            skLineSegment(sketch, "E190.MirrorCS", {"start": v(56.5, -27.02) * mm, "end": v(56.5, -43.7) * mm});
            skPoint(sketch, "E191.MirrorP", {"position": v(79, 0) * mm});
            skLineSegment(sketch, "E192.MirrorCS", {"start": v(24.5, -9.34) * mm, "end": v(24.5, -26.02) * mm});
            skLineSegment(sketch, "E193.MirrorCS", {"start": v(68.5, 26.02) * mm, "end": v(68.5, 9.34) * mm});
            skLineSegment(sketch, "E194.MirrorCS", {"start": v(68.5, -9.34) * mm, "end": v(68.5, -26.02) * mm});
            skLineSegment(sketch, "E195.MirrorCS", {"start": v(24.5, 26.02) * mm, "end": v(24.5, 9.34) * mm});
            skLineSegment(sketch, "E196.MirrorCS", {"start": v(46.5, -27.02) * mm, "end": v(46.5, -43.7) * mm});
            skLineSegment(sketch, "E197.MirrorCS", {"start": v(45.5, 43.7) * mm, "end": v(35.5, 43.7) * mm});
            skLineSegment(sketch, "E198.MirrorCS", {"start": v(89.5, -27.02) * mm, "end": v(79.5, -27.02) * mm});
            skLineSegment(sketch, "E199.MirrorCS", {"start": v(89.5, 8.34) * mm, "end": v(79.5, 8.34) * mm});
            skLineSegment(sketch, "E200.MirrorCS", {"start": v(45.5, -27.02) * mm, "end": v(35.5, -27.02) * mm});
            skLineSegment(sketch, "E201.MirrorCS", {"start": v(45.5, 8.34) * mm, "end": v(35.5, 8.34) * mm});
            skPoint(sketch, "E202.MirrorP", {"position": v(68, 0) * mm});
            skLineSegment(sketch, "E203.MirrorCS", {"start": v(45.5, 27.02) * mm, "end": v(35.5, 27.02) * mm});
            skLineSegment(sketch, "E204.MirrorCS", {"start": v(89.5, -43.7) * mm, "end": v(79.5, -43.7) * mm});
            skLineSegment(sketch, "E205.MirrorCS", {"start": v(45.5, -8.34) * mm, "end": v(35.5, -8.34) * mm});
            skLineSegment(sketch, "E206.MirrorCS", {"start": v(45.5, -43.7) * mm, "end": v(35.5, -43.7) * mm});
            skLineSegment(sketch, "E207.MirrorCS", {"start": v(89.5, -8.34) * mm, "end": v(79.5, -8.34) * mm});
            skSolve(sketch);
        }
        {
            var Q0;
            Q0=makeQuery(id+"F8.imprint","IMPRINT",FACE,{"disambiguationData":[TD([[makeQuery(id+"F8.imprint","IMPRINT",EDGE,{"derivedFrom":sQuery(id+"F8.wireOp",EDGE,"E44.bottom")}),-1.0]])]});
            var Q1;
            Q1=makeQuery(id+"F8.imprint","IMPRINT",FACE,{"disambiguationData":[TD([[makeQuery(id+"F8.imprint","IMPRINT",EDGE,{"derivedFrom":sQuery(id+"F8.wireOp",EDGE,"E45.bottom")}),-1.0]])]});
            var Q2;
            Q2=makeQuery(id+"F8.imprint","IMPRINT",FACE,{"disambiguationData":[TD([[makeQuery(id+"F8.imprint","IMPRINT",EDGE,{"derivedFrom":sQuery(id+"F8.wireOp",EDGE,"E46.bottom")}),-1.0]])]});
            var Q3;
            Q3=makeQuery(id+"F8.imprint","IMPRINT",FACE,{"disambiguationData":[TD([[makeQuery(id+"F8.imprint","IMPRINT",EDGE,{"derivedFrom":sQuery(id+"F8.wireOp",EDGE,"E47.bottom")}),-1.0]])]});
            var Q4;
            Q4=makeQuery(id+"F8.imprint","IMPRINT",FACE,{"disambiguationData":[TD([[makeQuery(id+"F8.imprint","IMPRINT",EDGE,{"derivedFrom":sQuery(id+"F8.wireOp",EDGE,"E48.bottom")}),-1.0]])]});
            var Q5;
            Q5=makeQuery(id+"F8.imprint","IMPRINT",FACE,{"disambiguationData":[TD([[makeQuery(id+"F8.imprint","IMPRINT",EDGE,{"derivedFrom":sQuery(id+"F8.wireOp",EDGE,"E49.bottom")}),-1.0]])]});
            var Q6;
            Q6=makeQuery(id+"F8.imprint","IMPRINT",FACE,{"disambiguationData":[TD([[makeQuery(id+"F8.imprint","IMPRINT",EDGE,{"derivedFrom":sQuery(id+"F8.wireOp",EDGE,"E55.bottom")}),-1.0]])]});
            var Q7;
            Q7=makeQuery(id+"F8.imprint","IMPRINT",FACE,{"disambiguationData":[TD([[makeQuery(id+"F8.imprint","IMPRINT",EDGE,{"derivedFrom":sQuery(id+"F8.wireOp",EDGE,"E54.bottom")}),-1.0]])]});
            var Q8;
            Q8=makeQuery(id+"F8.imprint","IMPRINT",FACE,{"disambiguationData":[TD([[makeQuery(id+"F8.imprint","IMPRINT",EDGE,{"derivedFrom":sQuery(id+"F8.wireOp",EDGE,"E53.bottom")}),-1.0]])]});
            var Q9;
            Q9=makeQuery(id+"F8.imprint","IMPRINT",FACE,{"disambiguationData":[TD([[makeQuery(id+"F8.imprint","IMPRINT",EDGE,{"derivedFrom":sQuery(id+"F8.wireOp",EDGE,"E52.bottom")}),-1.0]])]});
            var Q10;
            Q10=makeQuery(id+"F8.imprint","IMPRINT",FACE,{"disambiguationData":[TD([[makeQuery(id+"F8.imprint","IMPRINT",EDGE,{"derivedFrom":sQuery(id+"F8.wireOp",EDGE,"E51.bottom")}),-1.0]])]});
            var Q11;
            Q11=makeQuery(id+"F8.imprint","IMPRINT",FACE,{"disambiguationData":[TD([[makeQuery(id+"F8.imprint","IMPRINT",EDGE,{"derivedFrom":sQuery(id+"F8.wireOp",EDGE,"E50.bottom")}),-1.0]])]});
            var Q12;
            Q12=makeQuery(id+"F8.imprint","IMPRINT",FACE,{"disambiguationData":[TD([[makeQuery(id+"F8.imprint","IMPRINT",EDGE,{"derivedFrom":sQuery(id+"F8.wireOp",EDGE,"E56.bottom")}),-1.0]])]});
            var Q13;
            Q13=makeQuery(id+"F8.imprint","IMPRINT",FACE,{"disambiguationData":[TD([[makeQuery(id+"F8.imprint","IMPRINT",EDGE,{"derivedFrom":sQuery(id+"F8.wireOp",EDGE,"E57.bottom")}),-1.0]])]});
            var Q14;
            Q14=makeQuery(id+"F8.imprint","IMPRINT",FACE,{"disambiguationData":[TD([[makeQuery(id+"F8.imprint","IMPRINT",EDGE,{"derivedFrom":sQuery(id+"F8.wireOp",EDGE,"E58.bottom")}),-1.0]])]});
            var Q15;
            Q15=makeQuery(id+"F8.imprint","IMPRINT",FACE,{"disambiguationData":[TD([[makeQuery(id+"F8.imprint","IMPRINT",EDGE,{"derivedFrom":sQuery(id+"F8.wireOp",EDGE,"E59.bottom")}),-1.0]])]});
            var Q16;
            Q16=makeQuery(id+"F8.imprint","IMPRINT",FACE,{"disambiguationData":[TD([[makeQuery(id+"F8.imprint","IMPRINT",EDGE,{"derivedFrom":sQuery(id+"F8.wireOp",EDGE,"E60.bottom")}),-1.0]])]});
            var Q17;
            Q17=makeQuery(id+"F8.imprint","IMPRINT",FACE,{"disambiguationData":[TD([[makeQuery(id+"F8.imprint","IMPRINT",EDGE,{"derivedFrom":sQuery(id+"F8.wireOp",EDGE,"E61.bottom")}),-1.0]])]});
            var Q18;
            Q18=makeQuery(id+"F8.imprint","IMPRINT",FACE,{"disambiguationData":[TD([[makeQuery(id+"F8.imprint","IMPRINT",EDGE,{"derivedFrom":sQuery(id+"F8.wireOp",EDGE,"E67.bottom")}),-1.0]])]});
            var Q19;
            Q19=makeQuery(id+"F8.imprint","IMPRINT",FACE,{"disambiguationData":[TD([[makeQuery(id+"F8.imprint","IMPRINT",EDGE,{"derivedFrom":sQuery(id+"F8.wireOp",EDGE,"E66.bottom")}),-1.0]])]});
            var Q20;
            Q20=makeQuery(id+"F8.imprint","IMPRINT",FACE,{"disambiguationData":[TD([[makeQuery(id+"F8.imprint","IMPRINT",EDGE,{"derivedFrom":sQuery(id+"F8.wireOp",EDGE,"E65.bottom")}),-1.0]])]});
            var Q21;
            Q21=makeQuery(id+"F8.imprint","IMPRINT",FACE,{"disambiguationData":[TD([[makeQuery(id+"F8.imprint","IMPRINT",EDGE,{"derivedFrom":sQuery(id+"F8.wireOp",EDGE,"E64.bottom")}),-1.0]])]});
            var Q22;
            Q22=makeQuery(id+"F8.imprint","IMPRINT",FACE,{"disambiguationData":[TD([[makeQuery(id+"F8.imprint","IMPRINT",EDGE,{"derivedFrom":sQuery(id+"F8.wireOp",EDGE,"E63.bottom")}),-1.0]])]});
            var Q23;
            Q23=makeQuery(id+"F8.imprint","IMPRINT",FACE,{"disambiguationData":[TD([[makeQuery(id+"F8.imprint","IMPRINT",EDGE,{"derivedFrom":sQuery(id+"F8.wireOp",EDGE,"E62.bottom")}),-1.0]])]});
            var Q24;
            Q24=makeQuery(id+"F8.imprint","IMPRINT",FACE,{"disambiguationData":[TD([[makeQuery(id+"F8.imprint","IMPRINT",EDGE,{"derivedFrom":sQuery(id+"F8.wireOp",EDGE,"E68.bottom")}),-1.0]])]});
            var Q25;
            Q25=makeQuery(id+"F8.imprint","IMPRINT",FACE,{"disambiguationData":[TD([[makeQuery(id+"F8.imprint","IMPRINT",EDGE,{"derivedFrom":sQuery(id+"F8.wireOp",EDGE,"E69.bottom")}),-1.0]])]});
            var Q26;
            Q26=makeQuery(id+"F8.imprint","IMPRINT",FACE,{"disambiguationData":[TD([[makeQuery(id+"F8.imprint","IMPRINT",EDGE,{"derivedFrom":sQuery(id+"F8.wireOp",EDGE,"E70.bottom")}),-1.0]])]});
            var Q27;
            Q27=makeQuery(id+"F8.imprint","IMPRINT",FACE,{"disambiguationData":[TD([[makeQuery(id+"F8.imprint","IMPRINT",EDGE,{"derivedFrom":sQuery(id+"F8.wireOp",EDGE,"E71.bottom")}),-1.0]])]});
            var Q28;
            Q28=makeQuery(id+"F8.imprint","IMPRINT",FACE,{"disambiguationData":[TD([[makeQuery(id+"F8.imprint","IMPRINT",EDGE,{"derivedFrom":sQuery(id+"F8.wireOp",EDGE,"E72.bottom")}),-1.0]])]});
            var Q29;
            Q29=makeQuery(id+"F8.imprint","IMPRINT",FACE,{"disambiguationData":[TD([[makeQuery(id+"F8.imprint","IMPRINT",EDGE,{"derivedFrom":sQuery(id+"F8.wireOp",EDGE,"E73.bottom")}),-1.0]])]});
            var Q30;
            Q30=makeQuery(id+"F8.imprint","IMPRINT",FACE,{"disambiguationData":[TD([[makeQuery(id+"F8.imprint","IMPRINT",EDGE,{"derivedFrom":sQuery(id+"F8.wireOp",EDGE,"E89.MirrorCS")}),1.0]])]});
            var Q31;
            Q31=makeQuery(id+"F8.imprint","IMPRINT",FACE,{"disambiguationData":[TD([[makeQuery(id+"F8.imprint","IMPRINT",EDGE,{"derivedFrom":sQuery(id+"F8.wireOp",EDGE,"E112.MirrorCS")}),-1.0]])]});
            var Q32;
            Q32=makeQuery(id+"F8.imprint","IMPRINT",FACE,{"disambiguationData":[TD([[makeQuery(id+"F8.imprint","IMPRINT",EDGE,{"derivedFrom":sQuery(id+"F8.wireOp",EDGE,"E168.MirrorCS")}),-1.0]])]});
            var Q33;
            Q33=makeQuery(id+"F8.imprint","IMPRINT",FACE,{"disambiguationData":[TD([[makeQuery(id+"F8.imprint","IMPRINT",EDGE,{"derivedFrom":sQuery(id+"F8.wireOp",EDGE,"E79.MirrorCS")}),1.0]])]});
            var Q34;
            Q34=makeQuery(id+"F8.imprint","IMPRINT",FACE,{"disambiguationData":[TD([[makeQuery(id+"F8.imprint","IMPRINT",EDGE,{"derivedFrom":sQuery(id+"F8.wireOp",EDGE,"E90.MirrorCS")}),1.0]])]});
            var Q35;
            Q35=makeQuery(id+"F8.imprint","IMPRINT",FACE,{"disambiguationData":[TD([[makeQuery(id+"F8.imprint","IMPRINT",EDGE,{"derivedFrom":sQuery(id+"F8.wireOp",EDGE,"E87.MirrorCS")}),1.0]])]});
            var Q36;
            Q36=makeQuery(id+"F8.imprint","IMPRINT",FACE,{"disambiguationData":[TD([[makeQuery(id+"F8.imprint","IMPRINT",EDGE,{"derivedFrom":sQuery(id+"F8.wireOp",EDGE,"E96.MirrorCS")}),-1.0]])]});
            var Q37;
            Q37=makeQuery(id+"F8.imprint","IMPRINT",FACE,{"disambiguationData":[TD([[makeQuery(id+"F8.imprint","IMPRINT",EDGE,{"derivedFrom":sQuery(id+"F8.wireOp",EDGE,"E176.MirrorCS")}),-1.0]])]});
            var Q38;
            Q38=makeQuery(id+"F8.imprint","IMPRINT",FACE,{"disambiguationData":[TD([[makeQuery(id+"F8.imprint","IMPRINT",EDGE,{"derivedFrom":sQuery(id+"F8.wireOp",EDGE,"E105.MirrorCS")}),1.0]])]});
            var Q39;
            Q39=makeQuery(id+"F8.imprint","IMPRINT",FACE,{"disambiguationData":[TD([[makeQuery(id+"F8.imprint","IMPRINT",EDGE,{"derivedFrom":sQuery(id+"F8.wireOp",EDGE,"E91.MirrorCS")}),-1.0]])]});
            var Q40;
            Q40=makeQuery(id+"F8.imprint","IMPRINT",FACE,{"disambiguationData":[TD([[makeQuery(id+"F8.imprint","IMPRINT",EDGE,{"derivedFrom":sQuery(id+"F8.wireOp",EDGE,"E99.MirrorCS")}),-1.0]])]});
            var Q41;
            Q41=makeQuery(id+"F8.imprint","IMPRINT",FACE,{"disambiguationData":[TD([[makeQuery(id+"F8.imprint","IMPRINT",EDGE,{"derivedFrom":sQuery(id+"F8.wireOp",EDGE,"E175.MirrorCS")}),-1.0]])]});
            var Q42;
            Q42=makeQuery(id+"F8.imprint","IMPRINT",FACE,{"disambiguationData":[TD([[makeQuery(id+"F8.imprint","IMPRINT",EDGE,{"derivedFrom":sQuery(id+"F8.wireOp",EDGE,"E78.MirrorCS")}),-1.0]])]});
            var Q43;
            Q43=makeQuery(id+"F8.imprint","IMPRINT",FACE,{"disambiguationData":[TD([[makeQuery(id+"F8.imprint","IMPRINT",EDGE,{"derivedFrom":sQuery(id+"F8.wireOp",EDGE,"E75.MirrorCS")}),1.0]])]});
            var Q44;
            Q44=makeQuery(id+"F8.imprint","IMPRINT",FACE,{"disambiguationData":[TD([[makeQuery(id+"F8.imprint","IMPRINT",EDGE,{"derivedFrom":sQuery(id+"F8.wireOp",EDGE,"E80.MirrorCS")}),-1.0]])]});
            var Q45;
            Q45=makeQuery(id+"F8.imprint","IMPRINT",FACE,{"disambiguationData":[TD([[makeQuery(id+"F8.imprint","IMPRINT",EDGE,{"derivedFrom":sQuery(id+"F8.wireOp",EDGE,"E77.MirrorCS")}),1.0]])]});
            var Q46;
            Q46=makeQuery(id+"F8.imprint","IMPRINT",FACE,{"disambiguationData":[TD([[makeQuery(id+"F8.imprint","IMPRINT",EDGE,{"derivedFrom":sQuery(id+"F8.wireOp",EDGE,"E92.MirrorCS")}),-1.0]])]});
            var Q47;
            Q47=makeQuery(id+"F8.imprint","IMPRINT",FACE,{"disambiguationData":[TD([[makeQuery(id+"F8.imprint","IMPRINT",EDGE,{"derivedFrom":sQuery(id+"F8.wireOp",EDGE,"E76.MirrorCS")}),1.0]])]});
            var Q48;
            Q48=makeQuery(id+"F8.imprint","IMPRINT",FACE,{"disambiguationData":[TD([[makeQuery(id+"F8.imprint","IMPRINT",EDGE,{"derivedFrom":sQuery(id+"F8.wireOp",EDGE,"E102.MirrorCS")}),1.0]])]});
            var Q49;
            Q49=makeQuery(id+"F8.imprint","IMPRINT",FACE,{"disambiguationData":[TD([[makeQuery(id+"F8.imprint","IMPRINT",EDGE,{"derivedFrom":sQuery(id+"F8.wireOp",EDGE,"E132.MirrorCS")}),1.0]])]});
            var Q50;
            Q50=makeQuery(id+"F8.imprint","IMPRINT",FACE,{"disambiguationData":[TD([[makeQuery(id+"F8.imprint","IMPRINT",EDGE,{"derivedFrom":sQuery(id+"F8.wireOp",EDGE,"E104.MirrorCS")}),1.0]])]});
            var Q51;
            Q51=makeQuery(id+"F8.imprint","IMPRINT",FACE,{"disambiguationData":[TD([[makeQuery(id+"F8.imprint","IMPRINT",EDGE,{"derivedFrom":sQuery(id+"F8.wireOp",EDGE,"E136.MirrorCS")}),1.0]])]});
            var Q52;
            Q52=makeQuery(id+"F8.imprint","IMPRINT",FACE,{"disambiguationData":[TD([[makeQuery(id+"F8.imprint","IMPRINT",EDGE,{"derivedFrom":sQuery(id+"F8.wireOp",EDGE,"E156.MirrorCS")}),1.0]])]});
            var Q53;
            Q53=makeQuery(id+"F8.imprint","IMPRINT",FACE,{"disambiguationData":[TD([[makeQuery(id+"F8.imprint","IMPRINT",EDGE,{"derivedFrom":sQuery(id+"F8.wireOp",EDGE,"E178.MirrorCS")}),-1.0]])]});
            var Q54;
            Q54=makeQuery(id+"F8.imprint","IMPRINT",FACE,{"disambiguationData":[TD([[makeQuery(id+"F8.imprint","IMPRINT",EDGE,{"derivedFrom":sQuery(id+"F8.wireOp",EDGE,"E109.MirrorCS")}),-1.0]])]});
            var Q55;
            Q55=makeQuery(id+"F8.imprint","IMPRINT",FACE,{"disambiguationData":[TD([[makeQuery(id+"F8.imprint","IMPRINT",EDGE,{"derivedFrom":sQuery(id+"F8.wireOp",EDGE,"E113.MirrorCS")}),-1.0]])]});
            var Q56;
            Q56=makeQuery(id+"F8.imprint","IMPRINT",FACE,{"disambiguationData":[TD([[makeQuery(id+"F8.imprint","IMPRINT",EDGE,{"derivedFrom":sQuery(id+"F8.wireOp",EDGE,"E85.MirrorCS")}),1.0]])]});
            var Q57;
            Q57=makeQuery(id+"F8.imprint","IMPRINT",FACE,{"disambiguationData":[TD([[makeQuery(id+"F8.imprint","IMPRINT",EDGE,{"derivedFrom":sQuery(id+"F8.wireOp",EDGE,"E119.MirrorCS")}),1.0]])]});
            var Q58;
            Q58=makeQuery(id+"F8.imprint","IMPRINT",FACE,{"disambiguationData":[TD([[makeQuery(id+"F8.imprint","IMPRINT",EDGE,{"derivedFrom":sQuery(id+"F8.wireOp",EDGE,"E84.MirrorCS")}),1.0]])]});
            var Q59;
            Q59=makeQuery(id+"F8.imprint","IMPRINT",FACE,{"disambiguationData":[TD([[makeQuery(id+"F8.imprint","IMPRINT",EDGE,{"derivedFrom":sQuery(id+"F8.wireOp",EDGE,"E119.MirrorCS")}),1.0]])]});
            var Q60;
            Q60=makeQuery(id+"F8.imprint","IMPRINT",FACE,{"disambiguationData":[TD([[makeQuery(id+"F8.imprint","IMPRINT",EDGE,{"derivedFrom":sQuery(id+"F8.wireOp",EDGE,"E129.MirrorCS")}),1.0]])]});
            extrude(context, id + "F9", {"entities" : qUnion([Q0, Q1, Q2, Q3, Q4, Q5, Q6, Q7, Q8, Q9, Q10, Q11, Q12, Q13, Q14, Q15, Q16, Q17, Q18, Q19, Q20, Q21, Q22, Q23, Q24, Q25, Q26, Q27, Q28, Q29, Q30, Q31, Q32, Q33, Q34, Q35, Q36, Q37, Q38, Q39, Q40, Q41, Q42, Q43, Q44, Q45, Q46, Q47, Q48, Q49, Q50, Q51, Q52, Q53, Q54, Q55, Q56, Q57, Q58, Q59, Q60]), "operationType" : NewBodyOperationType.REMOVE, "oppositeDirection" : true, "depth" : 6.1 * mm});
        }
    });
